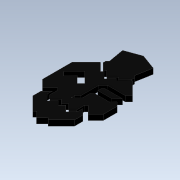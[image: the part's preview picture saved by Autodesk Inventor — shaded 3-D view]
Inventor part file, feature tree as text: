
AUTODESK INVENTOR PART (.ipt)
format: ipt  version: 2020 (Build 240168000, 168)  size: 335,872 bytes
history: native  units: in
note: dims shown in document units (in); Inventor stores cm internally (conversion verified against a paired STEP export)
features: extrude x2, sketch x2, projected_geometry x1
ambient origin geometry x8: Origin, YZ Plane, XZ Plane, XY Plane, X Axis, Y Axis, Z Axis, Center Point
bodies: Solid1 (feature_tree)
feature tree (5):
  extrude  "Extrusion1"  TaperAngle=90.0deg  [1 undecoded]
  extrude  "Extrusion2"  Depth=0.3937in
  sketch  "Sketch1"  dims[d0=0.3937in d1=90.0deg]
  sketch  "Sketch2"  dims[d2=45.0deg d3=0.0394in d4=0.5906in d5=90.0deg d6=0.3937in d7=0.5906in d8=90.0deg d9=0.1969in d10=0.3937in d11=45.0deg d12=0.5906in d13=0.3937in d14=45.0deg d15=0.5906in d16=90.0deg d17=0.3937in d18=90.0deg d19=0.3937in d20=90.0deg d21=0.5906in d22=90.0deg d23=0.5906in d24=90.0deg d25=0.5906in d26=0.5906in d27=0.3937in d28=0.5906in d29=45.0deg d30=0.5906in d31=45.0deg d32=0.3937in d33=0.5906in d34=135.0deg d35=1.1811in d36=1.1811in d37=135.0deg d38=0.1969in d39=135.0deg d40=90.0deg d41=0.7874in d42=0.1969in d43=0.7874in d44=135.0deg d45=0.1969in d46=0.4331in d47=0.1969in d48=45.0deg d49=0.1969in d50=90.0deg d51=0.7874in d52=0.7874in d53=90.0deg d54=0.5906in d55=0.5906in d56=0.1969in d57=135.0deg d58=0.7297in d59=0.3937in d60=0.3937in d61=45.0deg d62=45.0deg d63=0.1532in d64=0.1969in d65=0.1969in d66=0.7874in d67=0.4752in d68=135.0deg d69=0.9843in d70=135.0deg d71=0.3868in d72=0.3937in d73=135.0deg d74=0.3937in d75=135.0deg d76=90.0deg d77=0.689in d78=0.689in d79=1.0827in d80=1.0827in d81=3.937in d82=135.0deg d83=45.0deg d84=1.1832in d85=1.1832in d86=90.0deg d87=0.5906in d88=5.4304in d89=2.6102in d90=0.1462in d91=0.8608in d92=0.7129in d93=3.8974in d94=0.1969in d95=0.4524in d96=0.4524in d97=0.1969in d98=0.1969in d99=45.0deg d100=0.5906in d101=45.0deg d102=0.5906in d103=90.0deg d104=0.1968in d105=90.0deg d106=0.7087in d107=0.7087in d108=2.7839in d109=0.1969in d110=0.1969in d111=0.1969in d112=135.0deg d113=135.0deg d114=0.1969in d115=1.1811in d116=0.8589in d117=0.6871in d118=1.2598in d119=0.8589in d120=1.1811in d121=0.6871in d122=0.3937in d123=0.0in d124=0.3937in d125=0.0in d126=0.0197in d127=0.0344in]
  projected_geometry  "Projected Loop1"
note: 1 required parameter value undecoded (feature->parameter linkage not recoverable at this tier; creation-order binding heuristic only, values carry confidence <= 0.55)
